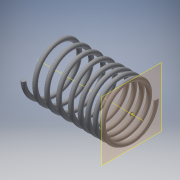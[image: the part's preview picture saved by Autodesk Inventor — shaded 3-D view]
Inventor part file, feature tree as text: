
AUTODESK INVENTOR PART (.ipt)
format: ipt  version: 2016 (Build 200138000, 138)  size: 374,272 bytes
history: native  units: in
note: dims shown in document units (in); Inventor stores cm internally (conversion verified against a paired STEP export)
features: sketch x4, extrude x2, helix x2
ambient origin geometry x8: Origin, YZ Plane, XZ Plane, XY Plane, X Axis, Y Axis, Z Axis, Center Point
bodies: Body1 (feature_tree)
feature tree (8):
  extrude  "Extrusion4"  Depth=0.315in TaperAngle=0.0deg
  helix  "Coil3"  [1 undecoded]
  extrude  "Extrusion5"  Depth=0.315in
  helix  "Coil4"  [1 undecoded]
  sketch  "Sketch6"  dims[d27=0.6457in d28=0.315in d29=0.0in d30=0.0591in]
  sketch  "Sketch7"  dims[d31=0.0295in d32=0.0787in d33=0.315in]
  sketch  "Sketch8"  dims[d34=1.5748in d35=0.0in d36=90.0deg d37=90.0deg d38=0.0in d39=0.0in d40=0.315in d41=0.7874in d42=0.0in]
  sketch  "Sketch9"  dims[d43=0.7874in d44=0.1181in d45=0.7874in d46=1.5748in d47=0.0in d48=90.0deg d49=90.0deg d50=0.0in d51=0.0in]
note: 2 required parameter values undecoded (feature->parameter linkage not recoverable at this tier; creation-order binding heuristic only, values carry confidence <= 0.55)
